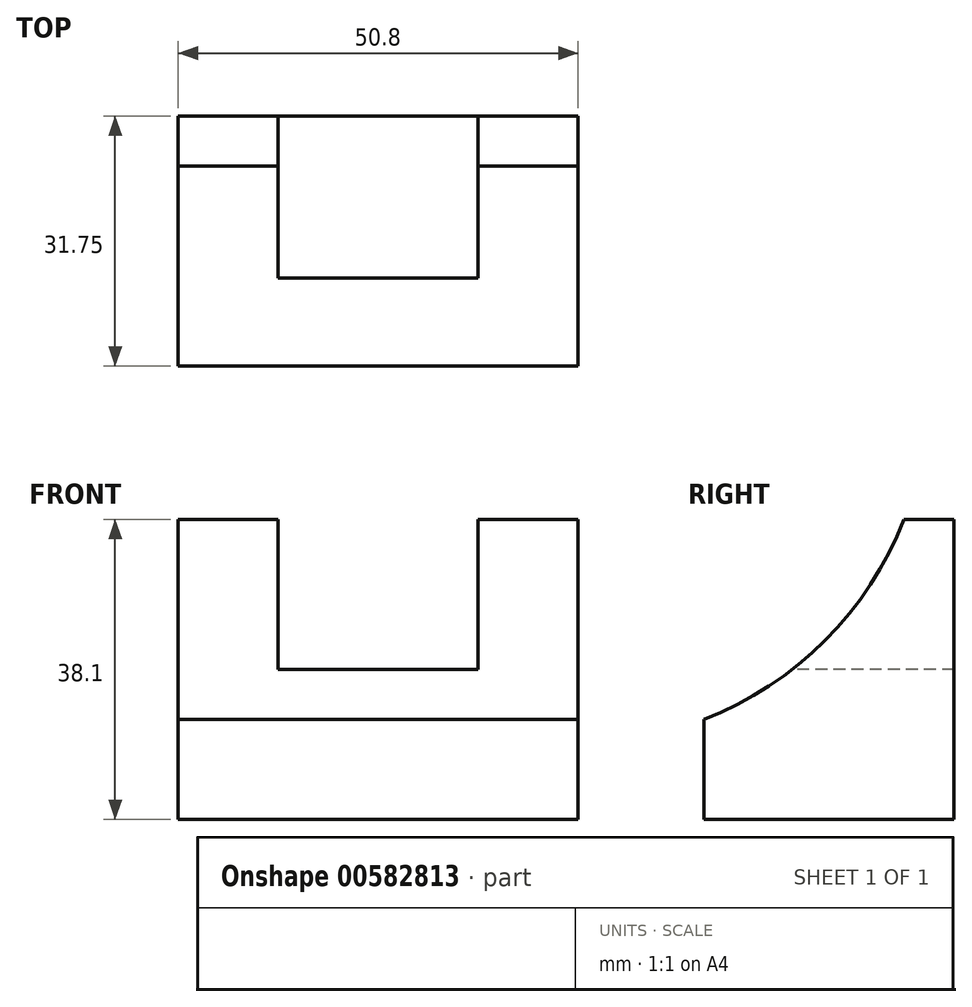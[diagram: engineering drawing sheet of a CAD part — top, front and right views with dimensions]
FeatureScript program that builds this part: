
annotation { "Feature Type Name" : "Feature", "Feature Type Description" : "" }
export const myFeature = defineFeature(function(context is Context, id is Id, definition is map)
    precondition{}
    {
        {
            var Q0;
            Q0=qCreatedBy(makeId("Front.planeOp"),FACE);
            var sketch = newSketch(context, id + "F0", { "sketchPlane" : qUnion([Q0])});
            skLineSegment(sketch, "E0", {"start": v(-70.54, 0) * mm, "end": v(-19.74, 0) * mm});
            skLineSegment(sketch, "E1", {"start": v(-19.74, 0) * mm, "end": v(-19.74, 38.1) * mm});
            skLineSegment(sketch, "E2", {"start": v(-19.74, 38.1) * mm, "end": v(-70.54, 38.1) * mm});
            skLineSegment(sketch, "E3", {"start": v(-70.54, 38.1) * mm, "end": v(-70.54, 0) * mm});
            skSolve(sketch);
        }
        {
            var Q0;
            Q0=makeQuery(id+"F0.imprint","IMPRINT",FACE,{"disambiguationData":[TD([[makeQuery(id+"F0.imprint","IMPRINT",EDGE,{"derivedFrom":sQuery(id+"F0.wireOp",EDGE,"E0")}),1.0]])]});
            extrude(context, id + "F1", {"entities" : qUnion([Q0]), "depth" : 31.75 * mm, "offsetDistance" : 25.4 * mm});
        }
        {
            var Q0;
            Q0=makeQuery(id+"F1.opExtrude","CAP_FACE",FACE,{"disambiguationData":[OSD([sQuery(id+"F0.wireOp",EDGE,"E0"),sQuery(id+"F0.wireOp",EDGE,"E1"),sQuery(id+"F0.wireOp",EDGE,"E2"),sQuery(id+"F0.wireOp",EDGE,"E3")])],"isStart":false});
            var sketch = newSketch(context, id + "F2", { "sketchPlane" : qUnion([Q0])});
            skLineSegment(sketch, "E4", {"start": v(-70.54, 38.1) * mm, "end": v(-57.84, 38.1) * mm});
            skLineSegment(sketch, "E5", {"start": v(-57.84, 38.1) * mm, "end": v(-57.84, 19.05) * mm});
            skLineSegment(sketch, "E6", {"start": v(-57.84, 19.05) * mm, "end": v(-32.44, 19.05) * mm});
            skLineSegment(sketch, "E7", {"start": v(-32.44, 19.05) * mm, "end": v(-32.44, 38.1) * mm});
            skLineSegment(sketch, "E8", {"start": v(-32.44, 38.1) * mm, "end": v(-19.74, 38.1) * mm});
            skSolve(sketch);
        }
        {
            var Q0;
            {var subQ0=sQuery(id+"F2.wireOp",EDGE,"E5");Q0=makeQuery(id+"F2.imprint","IMPRINT",FACE,{"disambiguationData":[TD([[makeQuery(id+"F2.imprint","IMPRINT",EDGE,{"derivedFrom":subQ0}),1.0]])]});}
            extrude(context, id + "F3", {"entities" : qUnion([Q0]), "operationType" : NewBodyOperationType.REMOVE, "oppositeDirection" : true, "depth" : 19.05 * mm, "offsetDistance" : 25.4 * mm});
        }
        {
            var Q0;
            Q0=makeQuery(id+"F3.boolean.opBoolean","COPY",FACE,{"derivedFrom":makeQuery(id+"F3.opExtrude","CAP_FACE",FACE,{"disambiguationData":[OSD([sQuery(id+"F0.wireOp",EDGE,"E2"),sQuery(id+"F2.wireOp",EDGE,"E5"),sQuery(id+"F2.wireOp",EDGE,"E6"),sQuery(id+"F2.wireOp",EDGE,"E7")])],"isStart":false})});
            extrude(context, id + "F4", {"entities" : qUnion([Q0]), "operationType" : NewBodyOperationType.REMOVE, "oppositeDirection" : true, "depth" : 25.4 * mm, "offsetDistance" : 25.4 * mm});
        }
        {
            var Q0;
            Q0=makeQuery(id+"F1.opExtrude","SWEPT_FACE",FACE,{"disambiguationData":[OSD([sQuery(id+"F0.wireOp",EDGE,"E1")])]});
            var sketch = newSketch(context, id + "F5", { "sketchPlane" : qUnion([Q0])});
            skLineSegment(sketch, "E9", {"start": v(0, 38.1) * mm, "end": v(-6.35, 38.1) * mm});
            skLineSegment(sketch, "E10", {"start": v(-31.75, 0) * mm, "end": v(-31.75, 12.7) * mm});
            skArc(sketch, "E11", {"start": v(-31.75, 12.7) * mm, "mid": v(-16.39, 22.74) * mm, "end": v(-6.35, 38.1) * mm});
            skSolve(sketch);
        }
        {
            var Q0;
            {var subQ0=sQuery(id+"F5.wireOp",EDGE,"E11");Q0=makeQuery(id+"F5.imprint","IMPRINT",FACE,{"disambiguationData":[TD([[makeQuery(id+"F5.imprint","IMPRINT",EDGE,{"derivedFrom":subQ0}),1.0]])]});}
            extrude(context, id + "F6", {"entities" : qUnion([Q0]), "operationType" : NewBodyOperationType.REMOVE, "oppositeDirection" : true, "depth" : 50.8 * mm, "offsetDistance" : 25.4 * mm});
        }
    });
